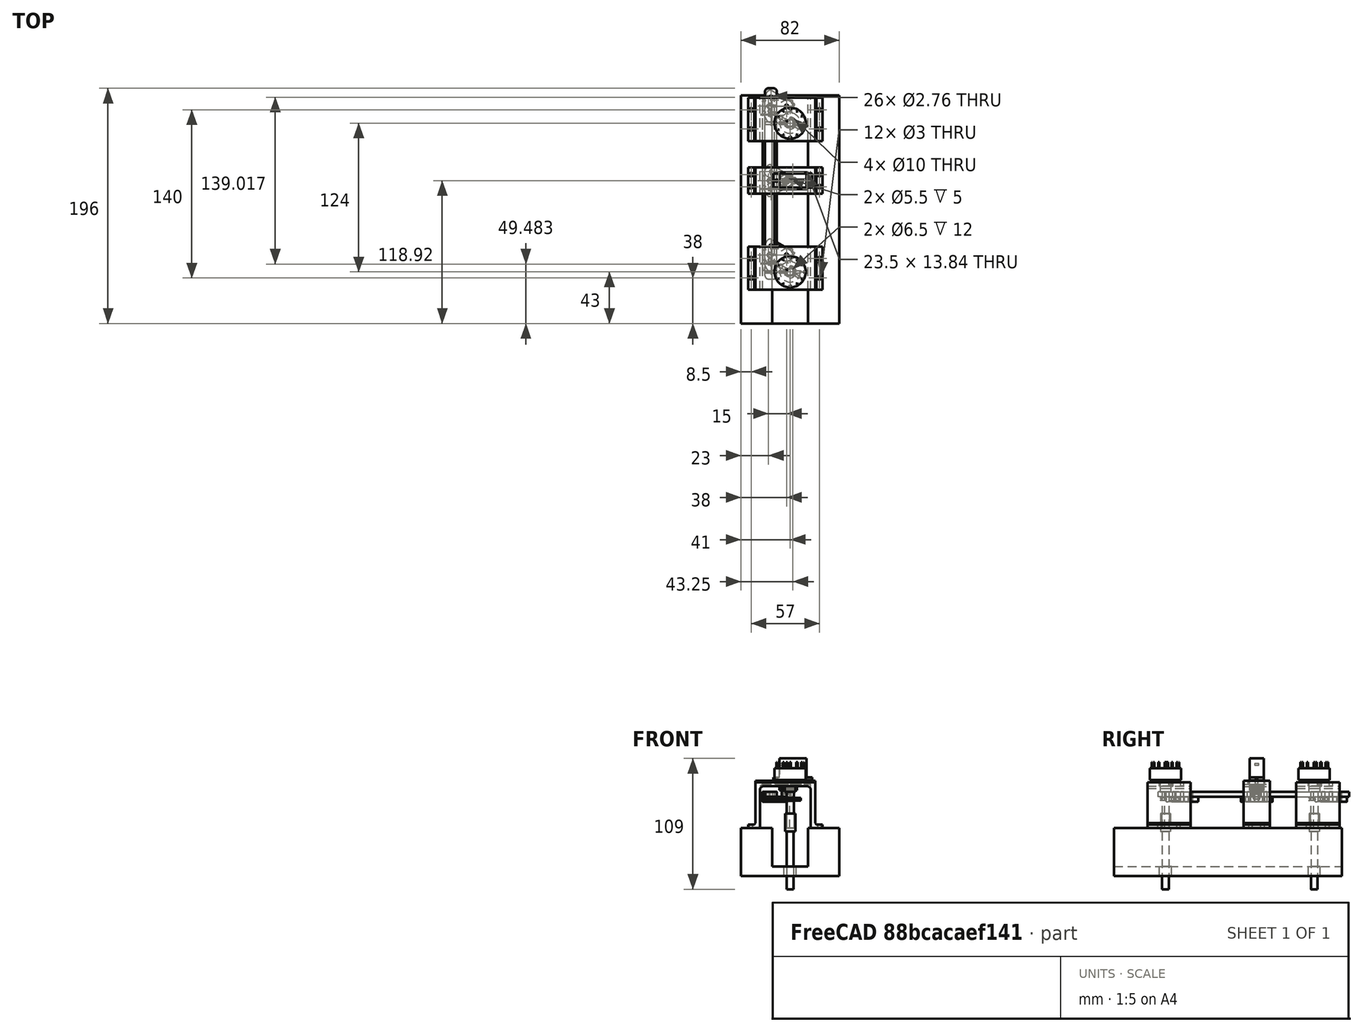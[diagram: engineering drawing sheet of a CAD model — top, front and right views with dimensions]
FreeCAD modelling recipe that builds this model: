
FCSTD DOCUMENT  (FreeCAD 0.17R13541 (Git))
Label: estructura rotary selector
License: All rights reserved
LicenseURL: http://en.wikipedia.org/wiki/All_rights_reserved
objects: Part::Cylinder×85, Part::Cut×62, Part::Box×43, Part::MultiFuse×13, Part::Fillet×12, Part::Chamfer×6, Part::FeaturePython×4, Mesh::Feature×4, Part::Feature×2
note: 227 computed .brp shape members not serialized (recipe doc carries the construction recipe); baked Part::Feature solids carry a one-line shape summary decoded from their .brp

FEATURE [Part::Cylinder] Cylinder001  label="Cuerpo 2"
  Angle = 360
  AttacherType = Attacher::AttachEngine3D
  Height = 2
  Placement = pos=(0,0,10) rot=(0,0,1;0rad)
  Radius = 8.5
FEATURE [Part::Cylinder] Cylinder  label="Cuerpo 1"
  Angle = 360
  AttacherType = Attacher::AttachEngine3D
  Height = 10
  Radius = 13
FEATURE [Part::Box] Box  label="Pin"
  AttacherType = Attacher::AttachEngine3D
  Height = 5
  Length = 0.5
  Placement = pos=(11,-0.5,-5) rot=(0,0,1;0rad)
  Width = 1
FEATURE [Part::Cylinder] Cylinder002  label="Cuerpo 3"
  Angle = 360
  AttacherType = Attacher::AttachEngine3D
  Height = 8
  Placement = pos=(0,0,12) rot=(0,0,1;0rad)
  Radius = 4.5
FEATURE [Part::Box] Box001  label="Pin central"
  AttacherType = Attacher::AttachEngine3D
  Height = 5
  Length = 0.5
  Placement = pos=(3,-0.5,-5) rot=(0,0,1;0rad)
  Width = 1
FEATURE [Part::Cylinder] Cylinder003  label="Cuerpo 4"
  Angle = 360
  AttacherType = Attacher::AttachEngine3D
  Height = 30
  Placement = pos=(0,0,20) rot=(0,0,1;0rad)
  Radius = 3
FEATURE [Part::Cylinder] Cylinder004  label="Cuerpo 5"
  Angle = 360
  AttacherType = Attacher::AttachEngine3D
  Height = 4
  Placement = pos=(9,0,10) rot=(0,0,1;0rad)
  Radius = 1.5
FEATURE [Part::Box] Box002  label="Recorte"
  AttacherType = Attacher::AttachEngine3D
  Height = 30
  Length = 1
  Placement = pos=(2,-5,20) rot=(0,0,1;0rad)
  Width = 10
FEATURE [Part::Cut] Cut  label="Cuerpo 4 recortado"
  Base = -> Cylinder003
  Refine = true
  Tool = -> Box002
FEATURE [Part::FeaturePython] Array  label="Pin array"  # Draft array (typed FeaturePython)
  Angle = 360
  ArrayType = 1
  Axis = (0,0,1)
  Base = -> Box
  Center = (0,0,0)
  Fuse = false
  IntervalAxis = (0,0,0)
  IntervalX = (1,0,0)
  IntervalY = (0,1,0)
  IntervalZ = (0,0,0)
  NumberPolar = 12
  NumberX = 2
  NumberY = 2
  NumberZ = 1
FEATURE [Part::MultiFuse] Fusion  label="Selector final 1"
  Placement = pos=(40.993,43.0109,90) rot=(0.258819,0.965926,0;3.14159rad)
  Refine = true
  Shapes = -> [Cylinder,Cylinder001,Array,Box001,Cylinder002,Cylinder004,Cut]
FEATURE [Part::Cylinder] Cylinder005  label="Cuerpo 006"
  Angle = 360
  AttacherType = Attacher::AttachEngine3D
  Height = 2
  Placement = pos=(0,0,10) rot=(0,0,1;0rad)
  Radius = 8.5
FEATURE [Part::Cylinder] Cylinder006  label="Cuerpo 007"
  Angle = 360
  AttacherType = Attacher::AttachEngine3D
  Height = 10
  Radius = 13
FEATURE [Part::Box] Box003  label="Pin001"
  AttacherType = Attacher::AttachEngine3D
  Height = 5
  Length = 0.5
  Placement = pos=(11,-0.5,-5) rot=(0,0,1;0rad)
  Width = 1
FEATURE [Part::Cylinder] Cylinder007  label="Cuerpo 008"
  Angle = 360
  AttacherType = Attacher::AttachEngine3D
  Height = 8
  Placement = pos=(0,0,12) rot=(0,0,1;0rad)
  Radius = 4.5
FEATURE [Part::Box] Box004  label="Pin central001"
  AttacherType = Attacher::AttachEngine3D
  Height = 5
  Length = 0.5
  Placement = pos=(3,-0.5,-5) rot=(0,0,1;0rad)
  Width = 1
FEATURE [Part::Cylinder] Cylinder008  label="Cuerpo 009"
  Angle = 360
  AttacherType = Attacher::AttachEngine3D
  Height = 30
  Placement = pos=(0,0,20) rot=(0,0,1;0rad)
  Radius = 3
FEATURE [Part::Cylinder] Cylinder009  label="Cuerpo 010"
  Angle = 360
  AttacherType = Attacher::AttachEngine3D
  Height = 4
  Placement = pos=(9,0,10) rot=(0,0,1;0rad)
  Radius = 1.5
FEATURE [Part::Box] Box005  label="Recorte001"
  AttacherType = Attacher::AttachEngine3D
  Height = 30
  Length = 1
  Placement = pos=(2,-5,20) rot=(0,0,1;0rad)
  Width = 10
FEATURE [Part::Cut] Cut001  label="Cuerpo 4 recortado001"
  Base = -> Cylinder008
  Refine = true
  Tool = -> Box005
FEATURE [Part::FeaturePython] Array001  label="Pin array001"  # Draft array (typed FeaturePython)
  Angle = 360
  ArrayType = 1
  Axis = (0,0,1)
  Base = -> Box003
  Center = (0,0,0)
  Fuse = false
  IntervalAxis = (0,0,0)
  IntervalX = (1,0,0)
  IntervalY = (0,1,0)
  IntervalZ = (0,0,0)
  NumberPolar = 12
  NumberX = 2
  NumberY = 2
  NumberZ = 1
FEATURE [Part::Box] Box006  label="Suelo"
  AttacherType = Attacher::AttachEngine3D
  Height = 8
  Length = 82
  Width = 190
FEATURE [Part::Box] Box007  label="Pared 2"
  AttacherType = Attacher::AttachEngine3D
  Height = 32
  Length = 26
  Placement = pos=(56,0,8) rot=(0,0,1;0rad)
  Width = 190
FEATURE [Part::Box] Box008  label="Pared 1"
  AttacherType = Attacher::AttachEngine3D
  Height = 32
  Length = 26
  Placement = pos=(0,0,8) rot=(0,0,1;0rad)
  Width = 190
FEATURE [Part::Cylinder] Cylinder010  label="Taladro 1"
  Angle = 360
  AttacherType = Attacher::AttachEngine3D
  Height = 16
  Placement = pos=(41,43,-4) rot=(0,0,1;0rad)
  Radius = 5
FEATURE [Part::Cylinder] Cylinder011  label="Taladro 2"
  Angle = 360
  AttacherType = Attacher::AttachEngine3D
  Height = 16
  Placement = pos=(41,167,-4) rot=(0,0,1;0rad)
  Radius = 5
FEATURE [Part::Cut] Cut002
  Base = -> Box006
  Refine = true
  Tool = -> Cylinder010
FEATURE [Part::Cut] Cut003  label="Suelo taladrado"
  Base = -> Cut002
  Refine = true
  Tool = -> Cylinder011
FEATURE [Part::Cylinder] Cylinder012  label="Cilindro"
  Angle = 360
  AttacherType = Attacher::AttachEngine3D
  Height = 15
  Radius = 4.25
FEATURE [Part::Cylinder] Cylinder013  label="taladro"
  Angle = 360
  AttacherType = Attacher::AttachEngine3D
  Height = 12
  Radius = 3.25
FEATURE [Part::Cut] Cut004  label="Cilindro exterior"
  Base = -> Cylinder012
  Refine = true
  Tool = -> Cylinder013
FEATURE [Part::Cylinder] Cylinder014  label="Cilindro interior"
  Angle = 360
  AttacherType = Attacher::AttachEngine3D
  Height = 48
  Placement = pos=(0,0,15) rot=(0,0,1;0rad)
  Radius = 2.75
FEATURE [Part::MultiFuse] Fusion003  label="Suelo final"
  Refine = true
  Shapes = -> [Box007,Box008,Cut003]
FEATURE [Mesh::Feature] Knob_v2_1  label="Knob 1"
  Placement = pos=(52.2,22.3,-2) rot=(-0.774597,-0.447214,0.447214;1.82348rad)
FEATURE [Mesh::Feature] Knob_v2_002  label="Knob 4"
  Placement = pos=(61,155,-1) rot=(-0.57735,-0.57735,0.57735;2.0944rad)
FEATURE [Part::MultiFuse] Fusion001  label="Selector final 2"
  Placement = pos=(40.993,166.974,90) rot=(0.258819,0.965926,0;3.14159rad)
  Refine = true
  Shapes = -> [Cylinder006,Cylinder005,Array001,Box004,Cylinder007,Cylinder009,Cut001]
FEATURE [Part::MultiFuse] Fusion002  label="Extensión selector 1"
  Placement = pos=(41,43,52) rot=(1,0,0;3.14159rad)
  Refine = true
  Shapes = -> [Cylinder014,Cut004]
FEATURE [Part::Cylinder] Cylinder015  label="Cilindro001"
  Angle = 360
  AttacherType = Attacher::AttachEngine3D
  Height = 15
  Radius = 4.25
FEATURE [Part::Cylinder] Cylinder016  label="taladro001"
  Angle = 360
  AttacherType = Attacher::AttachEngine3D
  Height = 12
  Radius = 3.25
FEATURE [Part::Cylinder] Cylinder017  label="Cilindro interior001"
  Angle = 360
  AttacherType = Attacher::AttachEngine3D
  Height = 48
  Placement = pos=(0,0,15) rot=(0,0,1;0rad)
  Radius = 2.75
FEATURE [Part::Cut] Cut005  label="Cilindro exterior001"
  Base = -> Cylinder015
  Refine = true
  Tool = -> Cylinder016
FEATURE [Part::MultiFuse] Fusion004  label="Extensión selector 2"
  Placement = pos=(41,167,52) rot=(1,0,0;3.14159rad)
  Refine = true
  Shapes = -> [Cylinder017,Cut005]
FEATURE [Part::Cylinder] Cylinder018  label="Varilla 1"
  Angle = 360
  AttacherType = Attacher::AttachEngine3D
  Height = 30
  Placement = pos=(23,53.5,64) rot=(0.250563,0.935113,-0.250563;1.63783rad)
  Radius = 1
FEATURE [Part::Cylinder] Cylinder019  label="Varilla 2"
  Angle = 360
  AttacherType = Attacher::AttachEngine3D
  Height = 30
  Placement = pos=(23,177.5,64) rot=(0.250563,0.935113,-0.250563;1.63783rad)
  Radius = 1
FEATURE [Part::Box] Box009  label="Base 1"
  AttacherType = Attacher::AttachEngine3D
  Height = 3
  Length = 50
  Placement = pos=(12,28,75) rot=(0,0,1;0rad)
  Width = 36
FEATURE [Part::Box] Box010  label="Pared 3"
  AttacherType = Attacher::AttachEngine3D
  Height = 38
  Length = 4
  Placement = pos=(12,28,40) rot=(0,0,1;0rad)
  Width = 36
FEATURE [Part::Box] Box011  label="Pared 4"
  AttacherType = Attacher::AttachEngine3D
  Height = 38
  Length = 4
  Placement = pos=(58,28,40) rot=(0,0,1;0rad)
  Width = 36
FEATURE [Part::Box] Box012  label="Base 2"
  AttacherType = Attacher::AttachEngine3D
  Height = 3
  Length = 10
  Placement = pos=(6,28,40) rot=(0,0,1;0rad)
  Width = 36
FEATURE [Part::Box] Box013  label="Base 3"
  AttacherType = Attacher::AttachEngine3D
  Height = 3
  Length = 10
  Placement = pos=(58,28,40) rot=(0,0,1;0rad)
  Width = 36
FEATURE [Part::MultiFuse] Fusion005  label="Soporte selector"
  Refine = true
  Shapes = -> [Box009,Box010,Box011,Box012,Box013]
FEATURE [Part::Chamfer] Chamfer
  Base = -> Fusion005
  Edges = 2 edges r=2: [Edge2,Edge4]
FEATURE [Part::Chamfer] Chamfer001  label="Estructura selector chaflan"
  Base = -> Chamfer
  Edges = 2 edges r=1: [Edge36,Edge42]
FEATURE [Part::Cylinder] Cylinder020  label="Taladro 3"
  Angle = 360
  AttacherType = Attacher::AttachEngine3D
  Height = 5
  Placement = pos=(8.5,38,39) rot=(0,0,1;0rad)
  Radius = 1.5
FEATURE [Part::Cylinder] Cylinder021  label="Taladro 4"
  Angle = 360
  AttacherType = Attacher::AttachEngine3D
  Height = 5
  Placement = pos=(8.5,54,39) rot=(0,0,1;0rad)
  Radius = 1.5
FEATURE [Part::Cylinder] Cylinder022  label="Taladro 5"
  Angle = 360
  AttacherType = Attacher::AttachEngine3D
  Height = 5
  Placement = pos=(65.5,38,39) rot=(0,0,1;0rad)
  Radius = 1.5
FEATURE [Part::Cylinder] Cylinder023  label="Taladro 6"
  Angle = 360
  AttacherType = Attacher::AttachEngine3D
  Height = 5
  Placement = pos=(65.5,54,39) rot=(0,0,1;0rad)
  Radius = 1.5
FEATURE [Part::Cut] Cut006
  Base = -> Chamfer001
  Refine = true
  Tool = -> Cylinder020
FEATURE [Part::Cut] Cut007
  Base = -> Cut006
  Refine = true
  Tool = -> Cylinder021
FEATURE [Part::Cut] Cut008
  Base = -> Cut007
  Refine = true
  Tool = -> Cylinder022
FEATURE [Part::Cut] Cut009  label="Estructura selector taladrada"
  Base = -> Cut008
  Refine = true
  Tool = -> Cylinder023
FEATURE [Part::Cylinder] Cylinder024  label="Cuerpo 011"
  Angle = 360
  AttacherType = Attacher::AttachEngine3D
  Height = 2
  Placement = pos=(0,0,10) rot=(0,0,1;0rad)
  Radius = 8.5
FEATURE [Part::Cylinder] Cylinder025  label="Cuerpo 012"
  Angle = 360
  AttacherType = Attacher::AttachEngine3D
  Height = 10
  Radius = 13
FEATURE [Part::Box] Box014  label="Pin002"
  AttacherType = Attacher::AttachEngine3D
  Height = 5
  Length = 0.5
  Placement = pos=(11,-0.5,-5) rot=(0,0,1;0rad)
  Width = 1
FEATURE [Part::FeaturePython] Array002  label="Pin array002"  # Draft array (typed FeaturePython)
  Angle = 360
  ArrayType = 1
  Axis = (0,0,1)
  Base = -> Box014
  Center = (0,0,0)
  Fuse = false
  IntervalAxis = (0,0,0)
  IntervalX = (1,0,0)
  IntervalY = (0,1,0)
  IntervalZ = (0,0,0)
  NumberPolar = 12
  NumberX = 2
  NumberY = 2
  NumberZ = 1
FEATURE [Part::Cylinder] Cylinder026  label="Cuerpo 013"
  Angle = 360
  AttacherType = Attacher::AttachEngine3D
  Height = 8
  Placement = pos=(0,0,12) rot=(0,0,1;0rad)
  Radius = 4.5
FEATURE [Part::Box] Box015  label="Pin central002"
  AttacherType = Attacher::AttachEngine3D
  Height = 5
  Length = 0.5
  Placement = pos=(3,-0.5,-5) rot=(0,0,1;0rad)
  Width = 1
FEATURE [Part::Cylinder] Cylinder027  label="Cuerpo 014"
  Angle = 360
  AttacherType = Attacher::AttachEngine3D
  Height = 30
  Placement = pos=(0,0,20) rot=(0,0,1;0rad)
  Radius = 3
FEATURE [Part::Cylinder] Cylinder028  label="Cuerpo 015"
  Angle = 360
  AttacherType = Attacher::AttachEngine3D
  Height = 4
  Placement = pos=(9,0,10) rot=(0,0,1;0rad)
  Radius = 1.5
FEATURE [Part::Box] Box016  label="Recorte002"
  AttacherType = Attacher::AttachEngine3D
  Height = 30
  Length = 1
  Placement = pos=(2,-5,20) rot=(0,0,1;0rad)
  Width = 10
FEATURE [Part::Cut] Cut010  label="Cuerpo 4 recortado002"
  Base = -> Cylinder027
  Refine = true
  Tool = -> Box016
FEATURE [Part::MultiFuse] Fusion006  label="Selector taladro"
  Placement = pos=(40.993,43.0109,90) rot=(0.258819,0.965926,0;3.14159rad)
  Refine = true
  Shapes = -> [Cylinder025,Cylinder024,Array002,Box015,Cylinder026,Cylinder028,Cut010]
FEATURE [Part::Cut] Cut011
  Base = -> Cut009
  Refine = true
  Tool = -> Fusion006
FEATURE [Part::Cylinder] Cylinder029  label="Taladro 007"
  Angle = 360
  AttacherType = Attacher::AttachEngine3D
  Height = 10
  Placement = pos=(41,43,71) rot=(0,0,1;0rad)
  Radius = 5
FEATURE [Part::Cylinder] Cylinder030  label="Taladro 008"
  Angle = 360
  AttacherType = Attacher::AttachEngine3D
  Height = 10
  Placement = pos=(33.25,47.5,71) rot=(0,0,1;0rad)
  Radius = 1.75
FEATURE [Part::Cut] Cut012
  Base = -> Cut011
  Refine = true
  Tool = -> Cylinder029
FEATURE [Part::Cut] Cut013  label="Base selector previa 1"
  Base = -> Cut012
  Refine = true
  Tool = -> Cylinder030
FEATURE [Part::Box] Box025  label="Palanca 1"
  AttacherType = Attacher::AttachEngine3D
  Height = 4
  Length = 25
  Placement = pos=(45,57,62) rot=(0,0,1;3.14159rad)
  Width = 10
FEATURE [Part::Cylinder] Cylinder042  label="Taladro 015"
  Angle = 360
  AttacherType = Attacher::AttachEngine3D
  Height = 10
  Placement = pos=(40,52,59) rot=(0,0,1;0rad)
  Radius = 1.38
FEATURE [Part::Cylinder] Cylinder043  label="Taladro 016"
  Angle = 360
  AttacherType = Attacher::AttachEngine3D
  Height = 10
  Placement = pos=(25,52,59) rot=(0,0,1;0rad)
  Radius = 1.38
FEATURE [Part::Cut] Cut022
  Base = -> Box025
  Refine = true
  Tool = -> Cylinder042
FEATURE [Part::Cut] Cut023  label="Palanca previa"
  Base = -> Cut022
  Refine = true
  Tool = -> Cylinder043
FEATURE [Part::Box] Box026  label="Palanca 002"
  AttacherType = Attacher::AttachEngine3D
  Height = 4
  Length = 25
  Placement = pos=(45,57,62) rot=(0,0,1;3.14159rad)
  Width = 10
FEATURE [Part::Cylinder] Cylinder044  label="Taladro 017"
  Angle = 360
  AttacherType = Attacher::AttachEngine3D
  Height = 10
  Placement = pos=(40,52,59) rot=(0,0,1;0rad)
  Radius = 1.38
FEATURE [Part::Cylinder] Cylinder045  label="Taladro 018"
  Angle = 360
  AttacherType = Attacher::AttachEngine3D
  Height = 10
  Placement = pos=(25,52,59) rot=(0,0,1;0rad)
  Radius = 1.38
FEATURE [Part::Cut] Cut025
  Base = -> Box026
  Refine = true
  Tool = -> Cylinder044
FEATURE [Part::Cut] Cut024  label="Palanca girada pos"
  Base = -> Cut025
  Placement = pos=(-20.65,26.95,0) rot=(0,0,-1;0.523599rad)
  Refine = true
  Tool = -> Cylinder045
FEATURE [Part::Box] Box027  label="Palanca 003"
  AttacherType = Attacher::AttachEngine3D
  Height = 4
  Length = 25
  Placement = pos=(45,57,62) rot=(0,0,1;3.14159rad)
  Width = 10
FEATURE [Part::Cylinder] Cylinder046  label="Taladro 019"
  Angle = 360
  AttacherType = Attacher::AttachEngine3D
  Height = 10
  Placement = pos=(40,52,59) rot=(0,0,1;0rad)
  Radius = 1.38
FEATURE [Part::Cylinder] Cylinder047  label="Taladro 020"
  Angle = 360
  AttacherType = Attacher::AttachEngine3D
  Height = 10
  Placement = pos=(25,52,59) rot=(0,0,1;0rad)
  Radius = 1.38
FEATURE [Part::Cut] Cut027
  Base = -> Box027
  Refine = true
  Tool = -> Cylinder046
FEATURE [Part::Cut] Cut026  label="Palanca girada neg"
  Base = -> Cut027
  Placement = pos=(31.35,-13.05,0) rot=(0,0,1;0.523599rad)
  Refine = true
  Tool = -> Cylinder047
FEATURE [Part::Cylinder] Cylinder048  label="Varilla  girada recta 1"
  Angle = 360
  AttacherType = Attacher::AttachEngine3D
  Height = 30
  Placement = pos=(20,43,64) rot=(0,1,0;1.5708rad)
  Radius = 1
FEATURE [Part::Fillet] Fillet  label="Palanca final 1"
  Base = -> Cut023
  Edges = 2 edges r=3: [Edge6,Edge13]
  Placement = pos=(-2,5,0) rot=(0,0,1;0rad)
FEATURE [Part::Fillet] Fillet001  label="Palanca final girada pos 1"
  Base = -> Cut024
  Edges = 2 edges r=3: [Edge6,Edge13]
  Placement = pos=(-2,5,0) rot=(0,0,1;0rad)
FEATURE [Part::Fillet] Fillet002  label="Palanca final girada neg 1"
  Base = -> Cut026
  Edges = 2 edges r=3: [Edge6,Edge13]
  Placement = pos=(-2,5,0) rot=(0,0,1;0rad)
FEATURE [Part::Cylinder] Cylinder049  label="Taladro 021"
  Angle = 360
  AttacherType = Attacher::AttachEngine3D
  Height = 40
  Placement = pos=(38,57,59) rot=(0,0,1;0rad)
  Radius = 1.38
FEATURE [Part::Cut] Cut028  label="Base selector final 1"
  Base = -> Cut013
  Refine = true
  Tool = -> Cylinder049
FEATURE [Part::Cylinder] Cylinder050  label="Cuerpo 016"
  Angle = 360
  AttacherType = Attacher::AttachEngine3D
  Height = 2
  Placement = pos=(0,0,10) rot=(0,0,1;0rad)
  Radius = 8.5
FEATURE [Part::Cylinder] Cylinder051  label="Cuerpo 017"
  Angle = 360
  AttacherType = Attacher::AttachEngine3D
  Height = 10
  Radius = 13
FEATURE [Part::Box] Box028  label="Pin003"
  AttacherType = Attacher::AttachEngine3D
  Height = 5
  Length = 0.5
  Placement = pos=(11,-0.5,-5) rot=(0,0,1;0rad)
  Width = 1
FEATURE [Part::Cylinder] Cylinder052  label="Cuerpo 018"
  Angle = 360
  AttacherType = Attacher::AttachEngine3D
  Height = 8
  Placement = pos=(0,0,12) rot=(0,0,1;0rad)
  Radius = 4.5
FEATURE [Part::Box] Box029  label="Pin central003"
  AttacherType = Attacher::AttachEngine3D
  Height = 5
  Length = 0.5
  Placement = pos=(3,-0.5,-5) rot=(0,0,1;0rad)
  Width = 1
FEATURE [Part::Cylinder] Cylinder053  label="Cuerpo 019"
  Angle = 360
  AttacherType = Attacher::AttachEngine3D
  Height = 30
  Placement = pos=(0,0,20) rot=(0,0,1;0rad)
  Radius = 3
FEATURE [Part::Cylinder] Cylinder054  label="Cuerpo 020"
  Angle = 360
  AttacherType = Attacher::AttachEngine3D
  Height = 4
  Placement = pos=(9,0,10) rot=(0,0,1;0rad)
  Radius = 1.5
FEATURE [Part::Box] Box030  label="Recorte003"
  AttacherType = Attacher::AttachEngine3D
  Height = 30
  Length = 1
  Placement = pos=(2,-5,20) rot=(0,0,1;0rad)
  Width = 10
FEATURE [Part::Box] Box031  label="Palanca 004"
  AttacherType = Attacher::AttachEngine3D
  Height = 4
  Length = 25
  Placement = pos=(45,57,62) rot=(0,0,1;3.14159rad)
  Width = 10
FEATURE [Part::Cylinder] Cylinder055  label="Taladro 022"
  Angle = 360
  AttacherType = Attacher::AttachEngine3D
  Height = 10
  Placement = pos=(40,52,59) rot=(0,0,1;0rad)
  Radius = 1.38
FEATURE [Part::Cylinder] Cylinder056  label="Taladro 023"
  Angle = 360
  AttacherType = Attacher::AttachEngine3D
  Height = 40
  Placement = pos=(38,57,59) rot=(0,0,1;0rad)
  Radius = 1.38
FEATURE [Part::FeaturePython] Array003  label="Pin array003"  # Draft array (typed FeaturePython)
  Angle = 360
  ArrayType = 1
  Axis = (0,0,1)
  Base = -> Box028
  Center = (0,0,0)
  Fuse = false
  IntervalAxis = (0,0,0)
  IntervalX = (1,0,0)
  IntervalY = (0,1,0)
  IntervalZ = (0,0,0)
  NumberPolar = 12
  NumberX = 2
  NumberY = 2
  NumberZ = 1
FEATURE [Part::Box] Box032  label="Base 004"
  AttacherType = Attacher::AttachEngine3D
  Height = 3
  Length = 10
  Placement = pos=(58,28,40) rot=(0,0,1;0rad)
  Width = 36
FEATURE [Part::Box] Box033  label="Base 005"
  AttacherType = Attacher::AttachEngine3D
  Height = 3
  Length = 50
  Placement = pos=(12,28,75) rot=(0,0,1;0rad)
  Width = 36
FEATURE [Part::Box] Box034  label="Pared 005"
  AttacherType = Attacher::AttachEngine3D
  Height = 38
  Length = 4
  Placement = pos=(12,28,40) rot=(0,0,1;0rad)
  Width = 36
FEATURE [Part::Box] Box035  label="Pared 006"
  AttacherType = Attacher::AttachEngine3D
  Height = 38
  Length = 4
  Placement = pos=(58,28,40) rot=(0,0,1;0rad)
  Width = 36
FEATURE [Part::Box] Box036  label="Base 006"
  AttacherType = Attacher::AttachEngine3D
  Height = 3
  Length = 10
  Placement = pos=(6,28,40) rot=(0,0,1;0rad)
  Width = 36
FEATURE [Part::MultiFuse] Fusion007  label="Soporte selector001"
  Refine = true
  Shapes = -> [Box033,Box034,Box035,Box036,Box032]
FEATURE [Part::Chamfer] Chamfer002
  Base = -> Fusion007
  Edges = 2 edges r=2: [Edge2,Edge4]
FEATURE [Part::Chamfer] Chamfer003  label="Estructura selector chaflan001"
  Base = -> Chamfer002
  Edges = 2 edges r=1: [Edge36,Edge42]
FEATURE [Part::Cylinder] Cylinder057  label="Taladro 024"
  Angle = 360
  AttacherType = Attacher::AttachEngine3D
  Height = 5
  Placement = pos=(8.5,38,39) rot=(0,0,1;0rad)
  Radius = 1.5
FEATURE [Part::Cut] Cut030
  Base = -> Chamfer003
  Refine = true
  Tool = -> Cylinder057
FEATURE [Part::Cylinder] Cylinder058  label="Taladro 025"
  Angle = 360
  AttacherType = Attacher::AttachEngine3D
  Height = 5
  Placement = pos=(8.5,54,39) rot=(0,0,1;0rad)
  Radius = 1.5
FEATURE [Part::Cut] Cut031
  Base = -> Cut030
  Refine = true
  Tool = -> Cylinder058
FEATURE [Part::Cylinder] Cylinder059  label="Taladro 026"
  Angle = 360
  AttacherType = Attacher::AttachEngine3D
  Height = 5
  Placement = pos=(65.5,38,39) rot=(0,0,1;0rad)
  Radius = 1.5
FEATURE [Part::Cut] Cut029
  Base = -> Cut031
  Refine = true
  Tool = -> Cylinder059
FEATURE [Part::Cylinder] Cylinder060  label="Taladro 027"
  Angle = 360
  AttacherType = Attacher::AttachEngine3D
  Height = 5
  Placement = pos=(65.5,54,39) rot=(0,0,1;0rad)
  Radius = 1.5
FEATURE [Part::Cylinder] Cylinder061  label="Taladro 028"
  Angle = 360
  AttacherType = Attacher::AttachEngine3D
  Height = 10
  Placement = pos=(25,52,59) rot=(0,0,1;0rad)
  Radius = 1.38
FEATURE [Part::Box] Box037  label="Palanca 005"
  AttacherType = Attacher::AttachEngine3D
  Height = 4
  Length = 25
  Placement = pos=(45,57,62) rot=(0,0,1;3.14159rad)
  Width = 10
FEATURE [Part::Cylinder] Cylinder062  label="Taladro 029"
  Angle = 360
  AttacherType = Attacher::AttachEngine3D
  Height = 10
  Placement = pos=(40,52,59) rot=(0,0,1;0rad)
  Radius = 1.38
FEATURE [Part::Cylinder] Cylinder063  label="Taladro 030"
  Angle = 360
  AttacherType = Attacher::AttachEngine3D
  Height = 10
  Placement = pos=(25,52,59) rot=(0,0,1;0rad)
  Radius = 1.38
FEATURE [Part::Box] Box038  label="Palanca 006"
  AttacherType = Attacher::AttachEngine3D
  Height = 4
  Length = 25
  Placement = pos=(45,57,62) rot=(0,0,1;3.14159rad)
  Width = 10
FEATURE [Part::Cylinder] Cylinder064  label="Taladro 031"
  Angle = 360
  AttacherType = Attacher::AttachEngine3D
  Height = 10
  Placement = pos=(40,52,59) rot=(0,0,1;0rad)
  Radius = 1.38
FEATURE [Part::Cylinder] Cylinder065  label="Taladro 032"
  Angle = 360
  AttacherType = Attacher::AttachEngine3D
  Height = 10
  Placement = pos=(25,52,59) rot=(0,0,1;0rad)
  Radius = 1.38
FEATURE [Part::Cut] Cut034
  Base = -> Box037
  Refine = true
  Tool = -> Cylinder062
FEATURE [Part::Cut] Cut035  label="Palanca girada pos001"
  Base = -> Cut034
  Placement = pos=(-20.65,26.95,0) rot=(0,0,-1;0.523599rad)
  Refine = true
  Tool = -> Cylinder063
FEATURE [Part::Fillet] Fillet003  label="Palanca final girada pos 2"
  Base = -> Cut035
  Edges = 2 edges r=3: [Edge6,Edge13]
  Placement = pos=(-2,129,0) rot=(0,0,1;0rad)
FEATURE [Part::Cut] Cut037
  Base = -> Box038
  Refine = true
  Tool = -> Cylinder064
FEATURE [Part::Cut] Cut036  label="Palanca girada neg001"
  Base = -> Cut037
  Placement = pos=(31.35,-13.05,0) rot=(0,0,1;0.523599rad)
  Refine = true
  Tool = -> Cylinder065
FEATURE [Part::Fillet] Fillet004  label="Palanca final girada neg 2"
  Base = -> Cut036
  Edges = 2 edges r=3: [Edge6,Edge13]
  Placement = pos=(-2,129,0) rot=(0,0,1;0rad)
FEATURE [Part::Cut] Cut038  label="Cuerpo 4 recortado003"
  Base = -> Cylinder053
  Refine = true
  Tool = -> Box030
FEATURE [Part::MultiFuse] Fusion008  label="Selector taladro001"
  Placement = pos=(40.993,43.0109,90) rot=(0.258819,0.965926,0;3.14159rad)
  Refine = true
  Shapes = -> [Cylinder051,Cylinder050,Array003,Box029,Cylinder052,Cylinder054,Cut038]
FEATURE [Part::Cylinder] Cylinder066  label="Taladro 033"
  Angle = 360
  AttacherType = Attacher::AttachEngine3D
  Height = 10
  Placement = pos=(41,43,71) rot=(0,0,1;0rad)
  Radius = 5
FEATURE [Part::Cylinder] Cylinder067  label="Taladro 034"
  Angle = 360
  AttacherType = Attacher::AttachEngine3D
  Height = 10
  Placement = pos=(33.25,47.5,71) rot=(0,0,1;0rad)
  Radius = 1.75
FEATURE [Part::Cylinder] Cylinder068  label="Varilla  girada recta 2"
  Angle = 360
  AttacherType = Attacher::AttachEngine3D
  Height = 30
  Placement = pos=(20,167,64) rot=(0,1,0;1.5708rad)
  Radius = 1
FEATURE [Part::Cut] Cut039  label="Estructura selector taladrada001"
  Base = -> Cut029
  Refine = true
  Tool = -> Cylinder060
FEATURE [Part::Cut] Cut040
  Base = -> Box031
  Refine = true
  Tool = -> Cylinder055
FEATURE [Part::Cut] Cut033  label="Palanca previa001"
  Base = -> Cut040
  Refine = true
  Tool = -> Cylinder061
FEATURE [Part::Fillet] Fillet005  label="Palanca final 2"
  Base = -> Cut033
  Edges = 2 edges r=3: [Edge6,Edge13]
  Placement = pos=(-2,129,0) rot=(0,0,1;0rad)
FEATURE [Part::Cut] Cut041
  Base = -> Cut039
  Refine = true
  Tool = -> Fusion008
FEATURE [Part::Cut] Cut043
  Base = -> Cut041
  Refine = true
  Tool = -> Cylinder066
FEATURE [Part::Cut] Cut042  label="Base selector previa 002"
  Base = -> Cut043
  Refine = true
  Tool = -> Cylinder067
FEATURE [Part::Cut] Cut032  label="Base selector final 2"
  Base = -> Cut042
  Placement = pos=(0,124,0) rot=(0,0,1;0rad)
  Refine = true
  Tool = -> Cylinder056
FEATURE [Part::Cylinder] Cylinder069  label="Taladro 035"
  Angle = 360
  AttacherType = Attacher::AttachEngine3D
  Height = 10
  Placement = pos=(40,52,59) rot=(0,0,1;0rad)
  Radius = 2.75
FEATURE [Part::Box] Box039  label="Palanca 007"
  AttacherType = Attacher::AttachEngine3D
  Height = 4
  Length = 25
  Placement = pos=(45,57,62) rot=(0,0,1;3.14159rad)
  Width = 10
FEATURE [Part::Cut] Cut046
  Base = -> Box039
  Refine = true
  Tool = -> Cylinder069
FEATURE [Part::Cylinder] Cylinder070  label="Taladro 036"
  Angle = 360
  AttacherType = Attacher::AttachEngine3D
  Height = 10
  Placement = pos=(25,52,59) rot=(0,0,1;0rad)
  Radius = 1.38
FEATURE [Part::Cylinder] Cylinder071  label="Taladro 037"
  Angle = 360
  AttacherType = Attacher::AttachEngine3D
  Height = 10
  Placement = pos=(25,52,59) rot=(0,0,1;0rad)
  Radius = 1.38
FEATURE [Part::Cut] Cut049  label="Palanca girada pos002"
  Base = -> Cut046
  Placement = pos=(-20.65,26.95,0) rot=(0,0,-1;0.523599rad)
  Refine = true
  Tool = -> Cylinder071
FEATURE [Part::Cylinder] Cylinder072  label="Taladro 038"
  Angle = 360
  AttacherType = Attacher::AttachEngine3D
  Height = 10
  Placement = pos=(40,52,59) rot=(0,0,1;0rad)
  Radius = 2.25
FEATURE [Part::Box] Box040  label="Palanca 008"
  AttacherType = Attacher::AttachEngine3D
  Height = 4
  Length = 25
  Placement = pos=(45,57,62) rot=(0,0,1;3.14159rad)
  Width = 10
FEATURE [Part::Cut] Cut047
  Base = -> Box040
  Refine = true
  Tool = -> Cylinder072
FEATURE [Part::Cut] Cut048  label="Palanca girada neg002"
  Base = -> Cut047
  Placement = pos=(31.35,-13.05,0) rot=(0,0,1;0.523599rad)
  Refine = true
  Tool = -> Cylinder070
FEATURE [Part::Cylinder] Cylinder073  label="Taladro 039"
  Angle = 360
  AttacherType = Attacher::AttachEngine3D
  Height = 10
  Placement = pos=(25,52,59) rot=(0,0,1;0rad)
  Radius = 1.38
FEATURE [Part::Fillet] Fillet006  label="Palanca girada pos 3"
  Base = -> Cut049
  Edges = 2 edges r=3: [Edge6,Edge13]
  Placement = pos=(-2,67,0) rot=(0,0,1;0rad)
FEATURE [Part::Fillet] Fillet007  label="Palanca girada neg 3"
  Base = -> Cut048
  Edges = 2 edges r=3: [Edge6,Edge13]
  Placement = pos=(-2,67,0) rot=(0,0,1;0rad)
FEATURE [Part::Box] Box041  label="Palanca 009"
  AttacherType = Attacher::AttachEngine3D
  Height = 4
  Length = 25
  Placement = pos=(45,57,62) rot=(0,0,1;3.14159rad)
  Width = 10
FEATURE [Part::Cylinder] Cylinder074  label="Taladro 040"
  Angle = 360
  AttacherType = Attacher::AttachEngine3D
  Height = 10
  Placement = pos=(40,52,59) rot=(0,0,1;0rad)
  Radius = 2.25
FEATURE [Part::Cut] Cut044
  Base = -> Box041
  Refine = true
  Tool = -> Cylinder074
FEATURE [Part::Cut] Cut045  label="Palanca previa002"
  Base = -> Cut044
  Refine = true
  Tool = -> Cylinder073
FEATURE [Part::Fillet] Fillet008  label="Palanca 3"
  Base = -> Cut045
  Edges = 2 edges r=3: [Edge6,Edge13]
  Placement = pos=(-2,67,0) rot=(0,0,1;0rad)
FEATURE [Part::Box] Box042  label="Unión palancas"
  AttacherType = Attacher::AttachEngine3D
  Height = 4
  Length = 10
  Placement = pos=(20,51,66) rot=(0,0,1;0rad)
  Width = 145
FEATURE [Part::Fillet] Fillet009  label="Unión placas chaflanado"
  Base = -> Box042
  Edges = 4 edges r=3: [Edge1,Edge3,Edge5,Edge7]
FEATURE [Part::Cylinder] Cylinder075  label="Taladro 041"
  Angle = 360
  AttacherType = Attacher::AttachEngine3D
  Height = 13
  Placement = pos=(25,64.5,59) rot=(0,0,1;0rad)
  Radius = 1.38
FEATURE [Part::Cylinder] Cylinder076  label="Taladro 042"
  Angle = 360
  AttacherType = Attacher::AttachEngine3D
  Height = 13
  Placement = pos=(25,126.5,59) rot=(0,0,1;0rad)
  Radius = 1.38
FEATURE [Part::Cylinder] Cylinder077  label="Taladro 043"
  Angle = 360
  AttacherType = Attacher::AttachEngine3D
  Height = 13
  Placement = pos=(25,188.5,59) rot=(0,0,1;0rad)
  Radius = 1.38
FEATURE [Part::Cut] Cut050
  Base = -> Fillet009
  Refine = true
  Tool = -> Cylinder075
FEATURE [Part::Cut] Cut051
  Base = -> Cut050
  Refine = true
  Tool = -> Cylinder076
FEATURE [Part::Cut] Cut052  label="Unión palancas final pos"
  Base = -> Cut051
  Refine = true
  Tool = -> Cylinder077
FEATURE [Part::Feature] Servo_SG90001_solid002  label="Servo"
  Placement = pos=(59.1,113,80) rot=(0,1,0;3.14159rad)
  shape: bbox 32.4 x 11.8 x 29.9 mm, 2326 faces (baked)
FEATURE [Part::Cylinder] Cylinder078  label="Extensión 1"
  Angle = 360
  AttacherType = Attacher::AttachEngine3D
  Height = 9
  Placement = pos=(17,17,10) rot=(0,0,1;0rad)
  Radius = 4
FEATURE [Part::Cylinder] Cylinder081  label="Cilindro002"
  Angle = 360
  AttacherType = Attacher::AttachEngine3D
  Height = 7
  Placement = pos=(17,17,12) rot=(0,0,1;0rad)
  Radius = 2.75
FEATURE [Part::Cut] Cut053  label="Extensión servo"
  Base = -> Cylinder078
  Placement = pos=(21,102,52) rot=(0,0,1;0rad)
  Refine = true
  Tool = -> Cylinder081
FEATURE [Part::Cylinder] Cylinder082  label="Extensión 002"
  Angle = 360
  AttacherType = Attacher::AttachEngine3D
  Height = 9
  Placement = pos=(17,17,10) rot=(0,0,1;0rad)
  Radius = 4
FEATURE [Part::Cylinder] Cylinder083  label="Cilindro003"
  Angle = 360
  AttacherType = Attacher::AttachEngine3D
  Height = 7
  Placement = pos=(17,17,12) rot=(0,0,1;0rad)
  Radius = 2.75
FEATURE [Part::Cut] Cut054  label="Extensión servo001"
  Base = -> Cylinder082
  Placement = pos=(21,102,52) rot=(0,0,1;0rad)
  Refine = true
  Tool = -> Cylinder083
FEATURE [Part::Cylinder] Cylinder084  label="Extensión 003"
  Angle = 360
  AttacherType = Attacher::AttachEngine3D
  Height = 9
  Placement = pos=(17,17,10) rot=(0,0,1;0rad)
  Radius = 4
FEATURE [Part::Cylinder] Cylinder085  label="Cilindro004"
  Angle = 360
  AttacherType = Attacher::AttachEngine3D
  Height = 7
  Placement = pos=(17,17,12) rot=(0,0,1;0rad)
  Radius = 2.75
FEATURE [Part::Cut] Cut055  label="Extensión servo002"
  Base = -> Cylinder084
  Placement = pos=(21,102,52) rot=(0,0,1;0rad)
  Refine = true
  Tool = -> Cylinder085
FEATURE [Part::MultiFuse] Fusion009  label="Palanca final girada pos 3"
  Refine = true
  Shapes = -> [Fillet006,Cut053]
FEATURE [Part::MultiFuse] Fusion010  label="Palanca final girada neg 3"
  Refine = true
  Shapes = -> [Fillet007,Cut054]
FEATURE [Part::MultiFuse] Fusion011  label="Palanca 3 final"
  Refine = true
  Shapes = -> [Fillet008,Cut055]
FEATURE [Part::Cylinder] Cylinder086  label="Taladro 044"
  Angle = 360
  AttacherType = Attacher::AttachEngine3D
  Height = 13
  Placement = pos=(25,188.5,59) rot=(0,0,1;0rad)
  Radius = 1.38
FEATURE [Part::Cylinder] Cylinder087  label="Taladro 045"
  Angle = 360
  AttacherType = Attacher::AttachEngine3D
  Height = 13
  Placement = pos=(25,64.5,59) rot=(0,0,1;0rad)
  Radius = 1.38
FEATURE [Part::Box] Box043  label="Unión palancas001"
  AttacherType = Attacher::AttachEngine3D
  Height = 4
  Length = 10
  Placement = pos=(20,51,66) rot=(0,0,1;0rad)
  Width = 145
FEATURE [Part::Cylinder] Cylinder088  label="Taladro 046"
  Angle = 360
  AttacherType = Attacher::AttachEngine3D
  Height = 13
  Placement = pos=(25,126.5,59) rot=(0,0,1;0rad)
  Radius = 1.38
FEATURE [Part::Fillet] Fillet010  label="Unión placas chaflanado001"
  Base = -> Box043
  Edges = 4 edges r=3: [Edge1,Edge3,Edge5,Edge7]
FEATURE [Part::Cut] Cut056
  Base = -> Fillet010
  Refine = true
  Tool = -> Cylinder087
FEATURE [Part::Cut] Cut057
  Base = -> Cut056
  Refine = true
  Tool = -> Cylinder088
FEATURE [Part::Cut] Cut058  label="Unión placas final recta"
  Base = -> Cut057
  Placement = pos=(-2,-7.5,0) rot=(0,0,1;0rad)
  Refine = true
  Tool = -> Cylinder086
FEATURE [Part::Box] Box044  label="Base 7"
  AttacherType = Attacher::AttachEngine3D
  Height = 3
  Length = 50
  Placement = pos=(12,108,76.5) rot=(0,0,1;0rad)
  Width = 22
FEATURE [Part::Feature] Servo_SG90001_solid003  label="Servo taladro"
  Placement = pos=(59.1,113,80) rot=(0,1,0;3.14159rad)
  shape: bbox 32.4 x 11.8 x 29.9 mm, 2326 faces (baked)
FEATURE [Part::Cut] Cut059
  Base = -> Box044
  Refine = true
  Tool = -> Servo_SG90001_solid003
FEATURE [Part::Box] Box045  label="Base 007"
  AttacherType = Attacher::AttachEngine3D
  Height = 3
  Length = 23.5
  Placement = pos=(31.5,112,76.5) rot=(0,0,1;0rad)
  Width = 13.84
FEATURE [Part::Cut] Cut060  label="Base servo"
  Base = -> Cut059
  Refine = true
  Tool = -> Box045
FEATURE [Part::Cylinder] Cylinder089  label="Taladro 047"
  Angle = 360
  AttacherType = Attacher::AttachEngine3D
  Height = 10
  Placement = pos=(29.75,119,73) rot=(0,0,1;0rad)
  Radius = 1.13
FEATURE [Part::Cylinder] Cylinder090  label="Taladro 048"
  Angle = 360
  AttacherType = Attacher::AttachEngine3D
  Height = 10
  Placement = pos=(56.75,119,73) rot=(0,0,1;0rad)
  Radius = 1.13
FEATURE [Part::Cut] Cut061
  Base = -> Cut060
  Refine = true
  Tool = -> Cylinder089
FEATURE [Part::Cut] Cut062  label="Base servo taladrada"
  Base = -> Cut061
  Refine = true
  Tool = -> Cylinder090
FEATURE [Part::Box] Box046  label="Pared 7"
  AttacherType = Attacher::AttachEngine3D
  Height = 36.5
  Length = 4
  Placement = pos=(12,108,40) rot=(0,0,1;0rad)
  Width = 22
FEATURE [Part::Box] Box047  label="Pared 8"
  AttacherType = Attacher::AttachEngine3D
  Height = 36.5
  Length = 4
  Placement = pos=(58,108,40) rot=(0,0,1;0rad)
  Width = 22
FEATURE [Part::Box] Box048  label="Base 008"
  AttacherType = Attacher::AttachEngine3D
  Height = 3
  Length = 10
  Placement = pos=(6,108,40) rot=(0,0,1;0rad)
  Width = 22
FEATURE [Part::Box] Box049  label="Base 009"
  AttacherType = Attacher::AttachEngine3D
  Height = 3
  Length = 10
  Placement = pos=(58,108,40) rot=(0,0,1;0rad)
  Width = 22
FEATURE [Part::Cylinder] Cylinder091  label="Taladro 049"
  Angle = 360
  AttacherType = Attacher::AttachEngine3D
  Height = 5
  Placement = pos=(8.5,124,39) rot=(0,0,1;0rad)
  Radius = 1.5
FEATURE [Part::Cylinder] Cylinder092  label="Taladro 050"
  Angle = 360
  AttacherType = Attacher::AttachEngine3D
  Height = 5
  Placement = pos=(8.5,114,39) rot=(0,0,1;0rad)
  Radius = 1.5
FEATURE [Part::Cut] Cut063
  Base = -> Box048
  Refine = true
  Tool = -> Cylinder091
FEATURE [Part::Cut] Cut064
  Base = -> Cut063
  Refine = true
  Tool = -> Cylinder092
FEATURE [Part::Cylinder] Cylinder093  label="Taladro 051"
  Angle = 360
  AttacherType = Attacher::AttachEngine3D
  Height = 5
  Placement = pos=(65.5,114,39) rot=(0,0,1;0rad)
  Radius = 1.5
FEATURE [Part::Cylinder] Cylinder094  label="Taladro 052"
  Angle = 360
  AttacherType = Attacher::AttachEngine3D
  Height = 5
  Placement = pos=(65.5,124,39) rot=(0,0,1;0rad)
  Radius = 1.5
FEATURE [Part::Cut] Cut065
  Base = -> Box049
  Refine = true
  Tool = -> Cylinder093
FEATURE [Part::Cut] Cut066
  Base = -> Cut065
  Refine = true
  Tool = -> Cylinder094
FEATURE [Part::MultiFuse] Fusion012  label="Base servo previa"
  Refine = true
  Shapes = -> [Cut066,Cut064,Box047,Box046,Cut062]
FEATURE [Part::Chamfer] Chamfer004
  Base = -> Fusion012
  Edges = 1 edges r=2: [Edge35]
FEATURE [Part::Chamfer] Chamfer005  label="Base servo final"
  Base = -> Chamfer004
  Edges = 2 edges r=1: [Edge36,Edge56]
FEATURE [Mesh::Feature] Knob_v2_003  label="Knob 3"
  Placement = pos=(61,31,-1) rot=(-0.57735,-0.57735,0.57735;2.0944rad)
FEATURE [Mesh::Feature] Knob_v2_004  label="Knob 2"
  Placement = pos=(52.2,146.3,-2) rot=(-0.774597,-0.447214,0.447214;1.82348rad)
FEATURE [Part::Cylinder] Cylinder095  label="Taladro 053"
  Angle = 360
  AttacherType = Attacher::AttachEngine3D
  Height = 13
  Placement = pos=(25,188.5,59) rot=(0,0,1;0rad)
  Radius = 1.38
FEATURE [Part::Cylinder] Cylinder096  label="Taladro 054"
  Angle = 360
  AttacherType = Attacher::AttachEngine3D
  Height = 13
  Placement = pos=(25,64.5,59) rot=(0,0,1;0rad)
  Radius = 1.38
FEATURE [Part::Box] Box050  label="Unión palancas002"
  AttacherType = Attacher::AttachEngine3D
  Height = 4
  Length = 10
  Placement = pos=(20,51,66) rot=(0,0,1;0rad)
  Width = 145
FEATURE [Part::Cylinder] Cylinder097  label="Taladro 055"
  Angle = 360
  AttacherType = Attacher::AttachEngine3D
  Height = 13
  Placement = pos=(25,126.5,59) rot=(0,0,1;0rad)
  Radius = 1.38
FEATURE [Part::Fillet] Fillet011  label="Unión placas chaflanado002"
  Base = -> Box050
  Edges = 4 edges r=3: [Edge1,Edge3,Edge5,Edge7]
FEATURE [Part::Cut] Cut067
  Base = -> Fillet011
  Refine = true
  Tool = -> Cylinder096
FEATURE [Part::Cut] Cut068
  Base = -> Cut067
  Refine = true
  Tool = -> Cylinder097
FEATURE [Part::Cut] Cut069  label="Unión placas final neg"
  Base = -> Cut068
  Placement = pos=(0,-14,0) rot=(0,0,1;0rad)
  Refine = true
  Tool = -> Cylinder095
